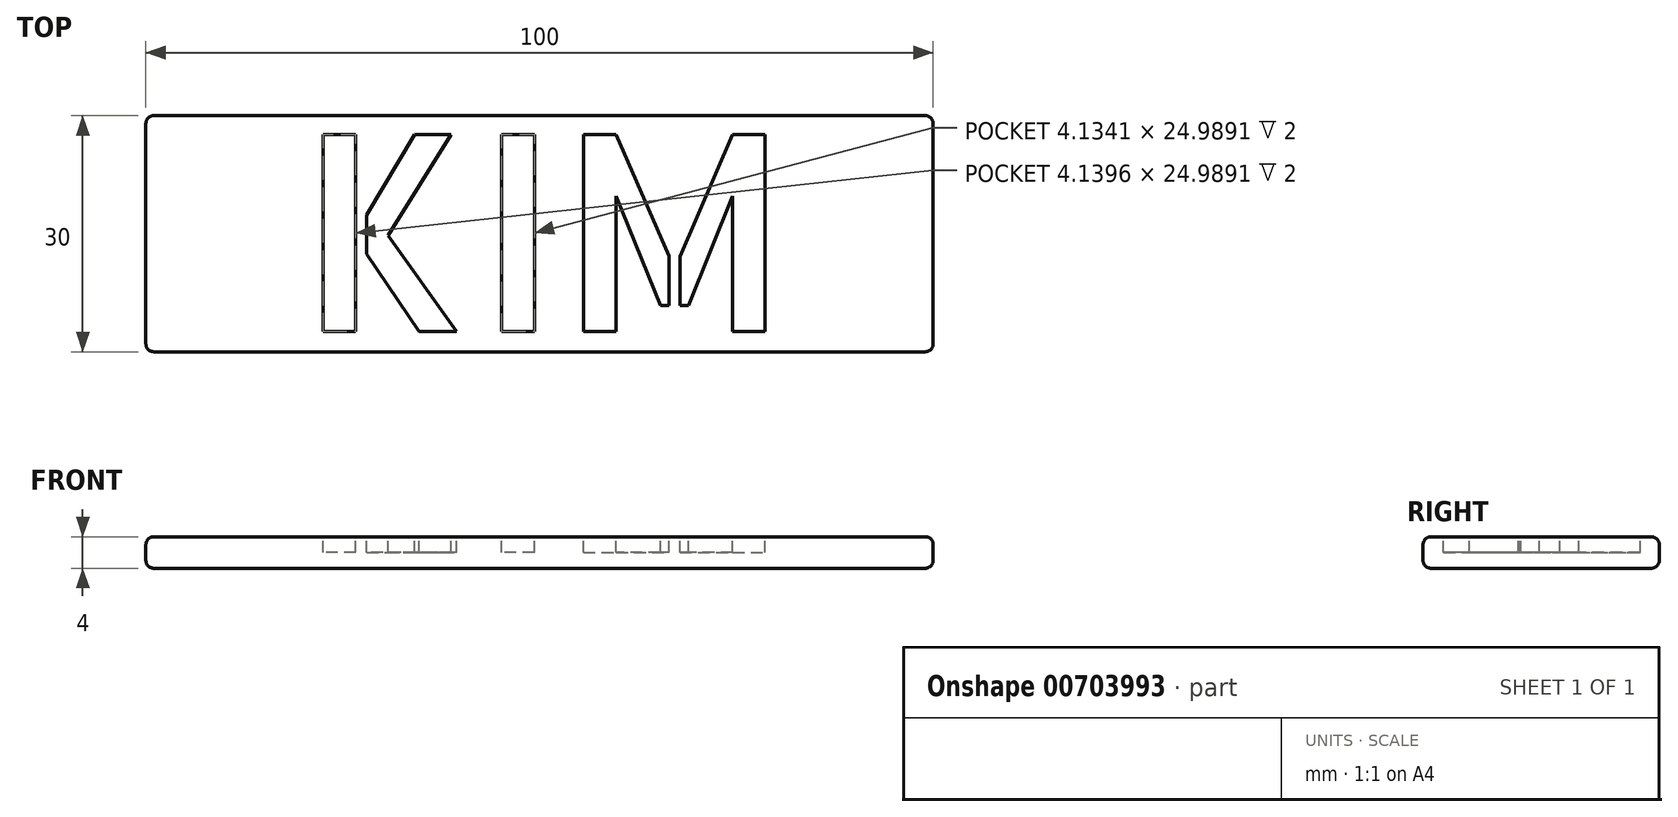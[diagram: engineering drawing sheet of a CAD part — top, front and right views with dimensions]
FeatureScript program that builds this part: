
annotation { "Feature Type Name" : "Feature", "Feature Type Description" : "" }
export const myFeature = defineFeature(function(context is Context, id is Id, definition is map)
    precondition{}
    {
        {
            var Q0;
            Q0=qCreatedBy(makeId("Top.planeOp"),FACE);
            var sketch = newSketch(context, id + "F0", { "sketchPlane" : qUnion([Q0])});
            skLineSegment(sketch, "E0.bottom", {"start": v(50, 15) * mm, "end": v(-50, 15) * mm});
            skLineSegment(sketch, "E0.top", {"start": v(50, -15) * mm, "end": v(-50, -15) * mm});
            skLineSegment(sketch, "E0.left", {"start": v(50, 15) * mm, "end": v(50, -15) * mm});
            skLineSegment(sketch, "E0.right", {"start": v(-50, 15) * mm, "end": v(-50, -15) * mm});
            skPoint(sketch, "E0.middle", {"position": v(0, 0) * mm});
            skSolve(sketch);
        }
        {
            var Q0;
            Q0=makeQuery(id+"F0.imprint","IMPRINT",FACE,{"disambiguationData":[TD([[makeQuery(id+"F0.imprint","IMPRINT",EDGE,{"derivedFrom":sQuery(id+"F0.wireOp",EDGE,"E0.bottom")}),1.0]])]});
            extrude(context, id + "F1", {"entities" : qUnion([Q0]), "oppositeDirection" : true, "depth" : 4 * mm, "offsetDistance" : 25 * mm});
        }
        {
            var Q0;
            Q0=makeQuery(id+"F1.opExtrude","CAP_EDGE",EDGE,{"disambiguationData":[OSD([sQuery(id+"F0.wireOp",EDGE,"E0.bottom")])],"isStart":true});
            var Q1;
            Q1=makeQuery(id+"F1.opExtrude","CAP_EDGE",EDGE,{"disambiguationData":[OSD([sQuery(id+"F0.wireOp",EDGE,"E0.bottom")])],"isStart":false});
            var Q2;
            Q2=makeQuery(id+"F1.opExtrude","CAP_EDGE",EDGE,{"disambiguationData":[OSD([sQuery(id+"F0.wireOp",EDGE,"E0.right")])],"isStart":true});
            var Q3;
            Q3=makeQuery(id+"F1.opExtrude","CAP_EDGE",EDGE,{"disambiguationData":[OSD([sQuery(id+"F0.wireOp",EDGE,"E0.right")])],"isStart":false});
            var Q4;
            Q4=makeQuery(id+"F1.opExtrude","SWEPT_EDGE",EDGE,{"disambiguationData":[OSD([sQuery(id+"F0.wireOp",EDGE,"E0.bottom"),sQuery(id+"F0.wireOp",EDGE,"E0.right")])]});
            var Q5;
            Q5=makeQuery(id+"F1.opExtrude","SWEPT_EDGE",EDGE,{"disambiguationData":[OSD([sQuery(id+"F0.wireOp",EDGE,"E0.bottom"),sQuery(id+"F0.wireOp",EDGE,"E0.left")])]});
            var Q6;
            Q6=makeQuery(id+"F1.opExtrude","CAP_EDGE",EDGE,{"disambiguationData":[OSD([sQuery(id+"F0.wireOp",EDGE,"E0.left")])],"isStart":false});
            var Q7;
            Q7=makeQuery(id+"F1.opExtrude","CAP_EDGE",EDGE,{"disambiguationData":[OSD([sQuery(id+"F0.wireOp",EDGE,"E0.left")])],"isStart":true});
            var Q8;
            Q8=makeQuery(id+"F1.opExtrude","SWEPT_EDGE",EDGE,{"disambiguationData":[OSD([sQuery(id+"F0.wireOp",EDGE,"E0.top"),sQuery(id+"F0.wireOp",EDGE,"E0.left")])]});
            var Q9;
            Q9=makeQuery(id+"F1.opExtrude","CAP_EDGE",EDGE,{"disambiguationData":[OSD([sQuery(id+"F0.wireOp",EDGE,"E0.top")])],"isStart":false});
            var Q10;
            Q10=makeQuery(id+"F1.opExtrude","CAP_EDGE",EDGE,{"disambiguationData":[OSD([sQuery(id+"F0.wireOp",EDGE,"E0.top")])],"isStart":true});
            var Q11;
            Q11=makeQuery(id+"F1.opExtrude","SWEPT_EDGE",EDGE,{"disambiguationData":[OSD([sQuery(id+"F0.wireOp",EDGE,"E0.top"),sQuery(id+"F0.wireOp",EDGE,"E0.right")])]});
            fillet(context, id + "F2", {"entities" : qUnion([Q0, Q1, Q2, Q3, Q4, Q5, Q6, Q7, Q8, Q9, Q10, Q11]), "radius" : 1 * mm, "tangentPropagation" : true, "allowEdgeOverflow" : false});
        }
        {
            var Q0;
            Q0=qCreatedBy(makeId("Top.planeOp"),FACE);
            var sketch = newSketch(context, id + "F3", { "sketchPlane" : qUnion([Q0])});
            skText(sketch, "E1", { "text": "KIM", "fontName": "AllertaStencil-Regular.ttf"});
            const initialGuessF3  = {"E1": [-0.03063, -0.0124, 1, 0, 0.025]};
            skSetInitialGuess(sketch, initialGuessF3);
            skSolve(sketch);
        }
        {
            var Q0;
            Q0 = qSketchRegion(id + "F3", true);
            extrude(context, id + "F4", {"entities" : qUnion([Q0]), "operationType" : NewBodyOperationType.REMOVE, "oppositeDirection" : true, "depth" : 2 * mm, "offsetDistance" : 25 * mm});
        }
    });
